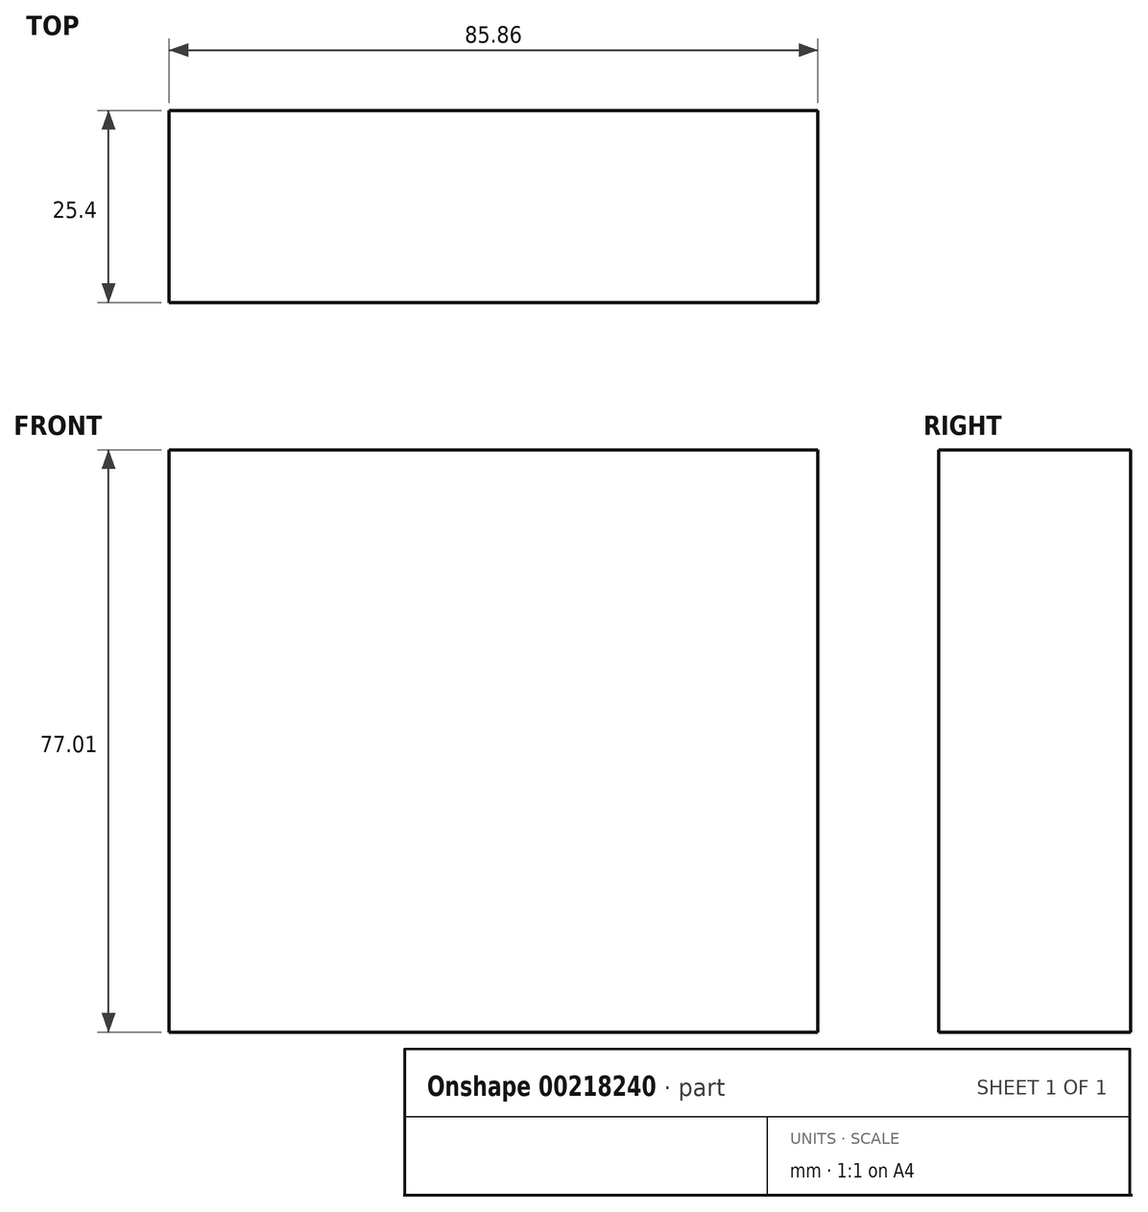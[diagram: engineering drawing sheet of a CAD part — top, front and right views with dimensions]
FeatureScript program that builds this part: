
annotation { "Feature Type Name" : "Feature", "Feature Type Description" : "" }
export const myFeature = defineFeature(function(context is Context, id is Id, definition is map)
    precondition{}
    {
        {
            var Q0;
            Q0=qCreatedBy(makeId("Front.planeOp"),FACE);
            var sketch = newSketch(context, id + "F0", { "sketchPlane" : qUnion([Q0])});
            skLineSegment(sketch, "E0.bottom", {"start": v(-37.37, 32.66) * mm, "end": v(48.5, 32.66) * mm});
            skLineSegment(sketch, "E0.top", {"start": v(-37.37, -44.35) * mm, "end": v(48.5, -44.35) * mm});
            skLineSegment(sketch, "E0.left", {"start": v(-37.37, 32.66) * mm, "end": v(-37.37, -44.35) * mm});
            skLineSegment(sketch, "E0.right", {"start": v(48.5, 32.66) * mm, "end": v(48.5, -44.35) * mm});
            skSolve(sketch);
        }
        {
            var Q0;
            Q0=makeQuery(id+"F0.imprint","IMPRINT",FACE,{"disambiguationData":[TD([[makeQuery(id+"F0.imprint","IMPRINT",EDGE,{"derivedFrom":sQuery(id+"F0.wireOp",EDGE,"E0.bottom")}),-1.0]])]});
            extrude(context, id + "F1", {"entities" : qUnion([Q0]), "depth" : 25.4 * mm});
        }
    });
